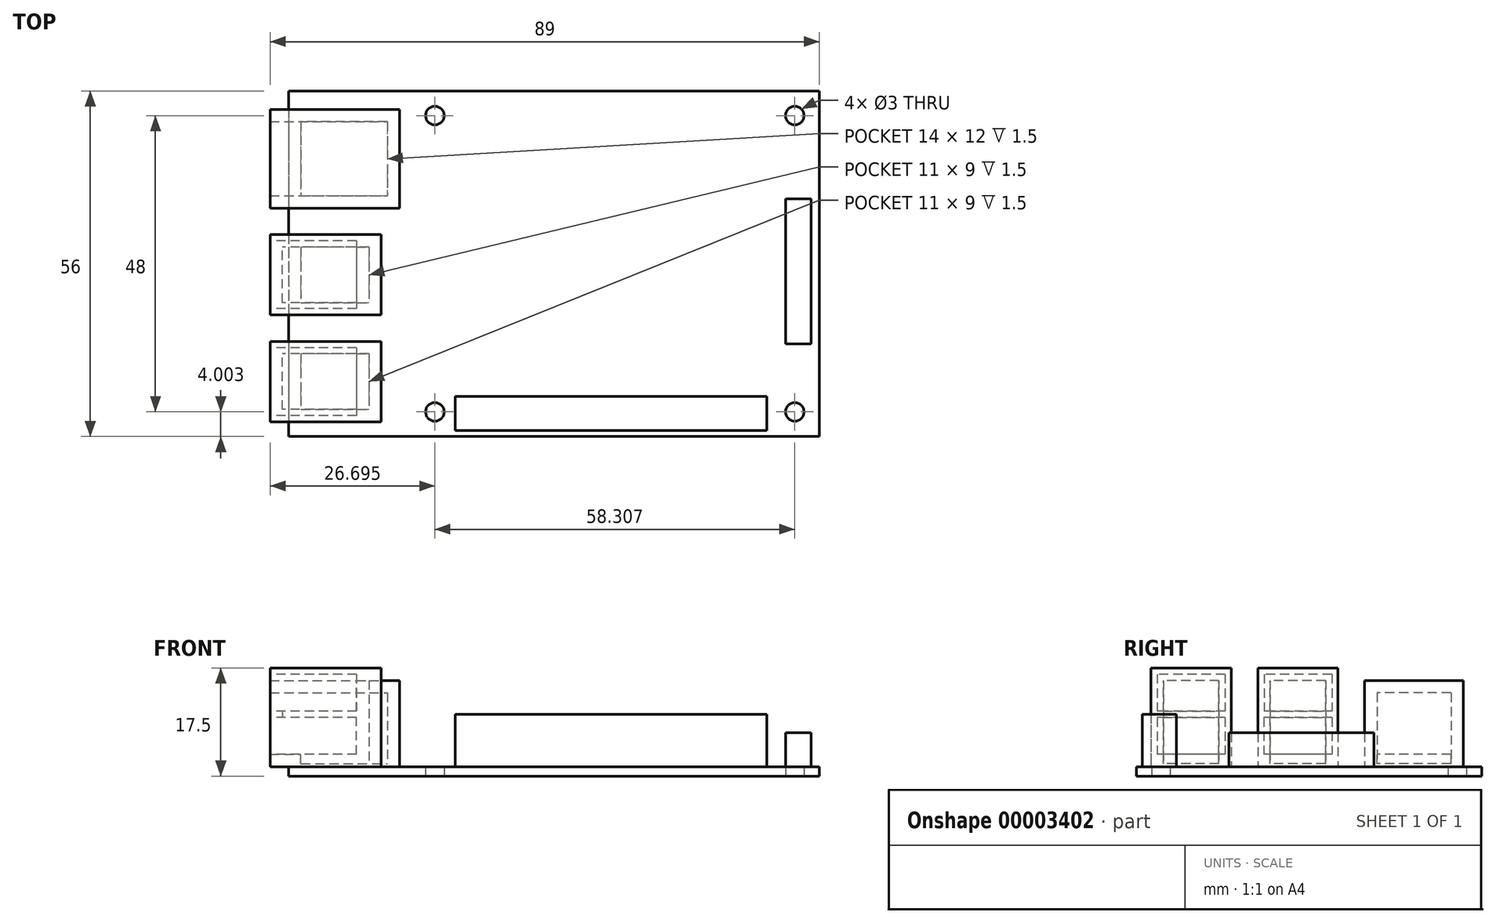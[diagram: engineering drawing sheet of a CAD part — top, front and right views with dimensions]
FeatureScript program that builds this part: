
annotation { "Feature Type Name" : "Feature", "Feature Type Description" : "" }
export const myFeature = defineFeature(function(context is Context, id is Id, definition is map)
    precondition{}
    {
        {
            var Q0;
            Q0=qCreatedBy(makeId("Top.planeOp"),FACE);
            var sketch = newSketch(context, id + "F0", { "sketchPlane" : qUnion([Q0])});
            skLineSegment(sketch, "E0.bottom", {"start": v(-78.39, -16) * mm, "end": v(7.61, -16) * mm});
            skLineSegment(sketch, "E0.top", {"start": v(-78.39, -72) * mm, "end": v(7.61, -72) * mm});
            skLineSegment(sketch, "E0.left", {"start": v(-78.39, -16) * mm, "end": v(-78.39, -72) * mm});
            skLineSegment(sketch, "E0.right", {"start": v(7.61, -16) * mm, "end": v(7.61, -72) * mm});
            skCircle(sketch, "E1", {"center": v(3.61, -20) * mm, "radius": 3 * mm, "construction": true});
            skCircle(sketch, "E2", {"center": v(3.61, -20) * mm, "radius": 1.5 * mm});
            skCircle(sketch, "E3.0.MirrorC", {"center": v(3.61, -68) * mm, "radius": 1.5 * mm});
            skCircle(sketch, "E3.1.MirrorC", {"center": v(3.61, -68) * mm, "radius": 3 * mm, "construction": true});
            skCircle(sketch, "E4.0.MirrorC", {"center": v(-54.7, -68) * mm, "radius": 3 * mm, "construction": true});
            skCircle(sketch, "E4.1.MirrorC", {"center": v(-54.7, -68) * mm, "radius": 1.5 * mm});
            skCircle(sketch, "E4.2.MirrorC", {"center": v(-54.7, -20) * mm, "radius": 1.5 * mm});
            skCircle(sketch, "E4.3.MirrorC", {"center": v(-54.7, -20) * mm, "radius": 3 * mm, "construction": true});
            skSolve(sketch);
        }
        {
            var Q0;
            Q0=makeQuery(id+"F0.imprint","IMPRINT",FACE,{"disambiguationData":[TD([[makeQuery(id+"F0.imprint","IMPRINT",EDGE,{"derivedFrom":sQuery(id+"F0.wireOp",EDGE,"E0.bottom")}),-1.0]])]});
            extrude(context, id + "F1", {"entities" : qUnion([Q0]), "depth" : 1.5 * mm});
        }
        {
            var Q0;
            Q0=makeQuery(id+"F1.opExtrude","CAP_FACE",FACE,{"disambiguationData":[OSD([sQuery(id+"F0.wireOp",EDGE,"E0.bottom"),sQuery(id+"F0.wireOp",EDGE,"E0.top"),sQuery(id+"F0.wireOp",EDGE,"E0.left"),sQuery(id+"F0.wireOp",EDGE,"E0.right"),sQuery(id+"F0.wireOp",EDGE,"E2"),sQuery(id+"F0.wireOp",EDGE,"E3.0.MirrorC"),sQuery(id+"F0.wireOp",EDGE,"E4.1.MirrorC"),sQuery(id+"F0.wireOp",EDGE,"E4.2.MirrorC")])],"isStart":false});
            var sketch = newSketch(context, id + "F2", { "sketchPlane" : qUnion([Q0])});
            skLineSegment(sketch, "E5.bottom", {"start": v(-81.39, -19) * mm, "end": v(-60.39, -19) * mm});
            skLineSegment(sketch, "E5.top", {"start": v(-81.39, -35) * mm, "end": v(-60.39, -35) * mm});
            skLineSegment(sketch, "E5.left", {"start": v(-81.39, -19) * mm, "end": v(-81.39, -35) * mm});
            skLineSegment(sketch, "E5.right", {"start": v(-60.39, -19) * mm, "end": v(-60.39, -35) * mm});
            skLineSegment(sketch, "E6.bottom", {"start": v(-81.39, -56.6) * mm, "end": v(-63.39, -56.6) * mm});
            skLineSegment(sketch, "E6.top", {"start": v(-81.39, -69.6) * mm, "end": v(-63.39, -69.6) * mm});
            skLineSegment(sketch, "E6.left", {"start": v(-81.39, -56.6) * mm, "end": v(-81.39, -69.6) * mm});
            skLineSegment(sketch, "E6.right", {"start": v(-63.39, -56.6) * mm, "end": v(-63.39, -69.6) * mm});
            skLineSegment(sketch, "E7.bottom", {"start": v(-81.39, -39.3) * mm, "end": v(-63.39, -39.3) * mm});
            skLineSegment(sketch, "E7.top", {"start": v(-81.39, -52.3) * mm, "end": v(-63.39, -52.3) * mm});
            skLineSegment(sketch, "E7.left", {"start": v(-81.39, -39.3) * mm, "end": v(-81.39, -52.3) * mm});
            skLineSegment(sketch, "E7.right", {"start": v(-63.39, -39.3) * mm, "end": v(-63.39, -52.3) * mm});
            skSolve(sketch);
        }
        {
            var Q0;
            {var subQ5=sQuery(id+"F2.wireOp",EDGE,"E5.right");Q0=makeQuery(id+"F2.imprint","IMPRINT",FACE,{"disambiguationData":[TD([[makeQuery(id+"F2.imprint","IMPRINT",EDGE,{"derivedFrom":subQ5}),-1.0]])]});}
            var Q1;
            {var subQ5=sQuery(id+"F2.wireOp",EDGE,"E5.left");Q1=makeQuery(id+"F2.imprint","IMPRINT",FACE,{"disambiguationData":[TD([[makeQuery(id+"F2.imprint","IMPRINT",EDGE,{"derivedFrom":subQ5}),1.0]])]});}
            extrude(context, id + "F3", {"entities" : qUnion([Q0, Q1]), "operationType" : NewBodyOperationType.ADD, "depth" : 14 * mm});
        }
        {
            var Q0;
            {var subQ5=sQuery(id+"F2.wireOp",EDGE,"E6.right");Q0=makeQuery(id+"F2.imprint","IMPRINT",FACE,{"disambiguationData":[TD([[makeQuery(id+"F2.imprint","IMPRINT",EDGE,{"derivedFrom":subQ5}),-1.0]])]});}
            var Q1;
            {var subQ5=sQuery(id+"F2.wireOp",EDGE,"E7.right");Q1=makeQuery(id+"F2.imprint","IMPRINT",FACE,{"disambiguationData":[TD([[makeQuery(id+"F2.imprint","IMPRINT",EDGE,{"derivedFrom":subQ5}),-1.0]])]});}
            var Q2;
            {var subQ5=sQuery(id+"F2.wireOp",EDGE,"E7.left");Q2=makeQuery(id+"F2.imprint","IMPRINT",FACE,{"disambiguationData":[TD([[makeQuery(id+"F2.imprint","IMPRINT",EDGE,{"derivedFrom":subQ5}),1.0]])]});}
            var Q3;
            {var subQ5=sQuery(id+"F2.wireOp",EDGE,"E6.left");Q3=makeQuery(id+"F2.imprint","IMPRINT",FACE,{"disambiguationData":[TD([[makeQuery(id+"F2.imprint","IMPRINT",EDGE,{"derivedFrom":subQ5}),1.0]])]});}
            extrude(context, id + "F4", {"entities" : qUnion([Q0, Q1, Q2, Q3]), "operationType" : NewBodyOperationType.ADD, "depth" : 16 * mm});
        }
        {
            var Q0;
            Q0=makeQuery(id+"F3.opExtrude","SWEPT_FACE",FACE,{"disambiguationData":[OSD([sQuery(id+"F2.wireOp",EDGE,"E5.left")])]});
            shell(context, id + "F5", {"entities" : qUnion([Q0]), "thickness" : 2 * mm});
        }
        {
            var Q0;
            {var subQ15=sQuery(id+"F2.wireOp",EDGE,"E5.right");Q0=makeQuery(id+"F2.imprint","IMPRINT",FACE,{"disambiguationData":[TD([[makeQuery(id+"F2.imprint","IMPRINT",EDGE,{"derivedFrom":subQ15}),1.0]])]});}
            var sketch = newSketch(context, id + "F6", { "sketchPlane" : qUnion([Q0])});
            skLineSegment(sketch, "E8.bottom", {"start": v(-51.39, -65.5) * mm, "end": v(-0.89, -65.5) * mm});
            skLineSegment(sketch, "E8.top", {"start": v(-51.39, -71) * mm, "end": v(-0.89, -71) * mm});
            skLineSegment(sketch, "E8.left", {"start": v(-51.39, -65.5) * mm, "end": v(-51.39, -71) * mm});
            skLineSegment(sketch, "E8.right", {"start": v(-0.89, -65.5) * mm, "end": v(-0.89, -71) * mm});
            skLineSegment(sketch, "E9.bottom", {"start": v(2.11, -33.5) * mm, "end": v(6.23, -33.5) * mm});
            skLineSegment(sketch, "E9.top", {"start": v(2.11, -56.97) * mm, "end": v(6.23, -56.97) * mm});
            skLineSegment(sketch, "E9.left", {"start": v(2.11, -33.5) * mm, "end": v(2.11, -56.97) * mm});
            skLineSegment(sketch, "E9.right", {"start": v(6.23, -33.5) * mm, "end": v(6.23, -56.97) * mm});
            skSolve(sketch);
        }
        {
            var Q0;
            Q0=makeQuery(id+"F6.imprint","IMPRINT",FACE,{"disambiguationData":[TD([[makeQuery(id+"F6.imprint","IMPRINT",EDGE,{"derivedFrom":sQuery(id+"F6.wireOp",EDGE,"E9.bottom")}),-1.0]])]});
            extrude(context, id + "F7", {"entities" : qUnion([Q0]), "operationType" : NewBodyOperationType.ADD, "depth" : 5.5 * mm});
        }
        {
            var Q0;
            Q0=makeQuery(id+"F6.imprint","IMPRINT",FACE,{"disambiguationData":[TD([[makeQuery(id+"F6.imprint","IMPRINT",EDGE,{"derivedFrom":sQuery(id+"F6.wireOp",EDGE,"E8.bottom")}),-1.0]])]});
            extrude(context, id + "F8", {"entities" : qUnion([Q0]), "operationType" : NewBodyOperationType.ADD, "depth" : 8.5 * mm});
        }
        {
            var Q0;
            Q0=makeQuery(id+"F4.opExtrude","SWEPT_FACE",FACE,{"disambiguationData":[OSD([sQuery(id+"F2.wireOp",EDGE,"E7.left")])]});
            var sketch = newSketch(context, id + "F9", { "sketchPlane" : qUnion([Q0])});
            skLineSegment(sketch, "E10.bottom", {"start": v(40.3, 16.5) * mm, "end": v(51.3, 16.5) * mm});
            skLineSegment(sketch, "E10.top", {"start": v(40.3, 10.5) * mm, "end": v(51.3, 10.5) * mm});
            skLineSegment(sketch, "E10.left", {"start": v(40.3, 16.5) * mm, "end": v(40.3, 10.5) * mm});
            skLineSegment(sketch, "E10.right", {"start": v(51.3, 16.5) * mm, "end": v(51.3, 10.5) * mm});
            skLineSegment(sketch, "E11.1.0.0", {"start": v(40.3, 3.5) * mm, "end": v(51.3, 3.5) * mm});
            skLineSegment(sketch, "E11.1.0.1", {"start": v(40.3, 9.5) * mm, "end": v(40.3, 3.5) * mm});
            skLineSegment(sketch, "E11.1.0.2", {"start": v(40.3, 9.5) * mm, "end": v(51.3, 9.5) * mm});
            skLineSegment(sketch, "E11.1.0.3", {"start": v(51.3, 9.5) * mm, "end": v(51.3, 3.5) * mm});
            skLineSegment(sketch, "E11.direction1", {"start": v(40.3, 10.5) * mm, "end": v(40.3, 3.5) * mm, "construction": true});
            skLineSegment(sketch, "E12.1.0.0", {"start": v(68.6, 16.5) * mm, "end": v(68.6, 10.5) * mm});
            skLineSegment(sketch, "E12.1.0.1", {"start": v(57.6, 16.5) * mm, "end": v(68.6, 16.5) * mm});
            skLineSegment(sketch, "E12.1.0.2", {"start": v(57.6, 3.5) * mm, "end": v(68.6, 3.5) * mm});
            skLineSegment(sketch, "E12.1.0.3", {"start": v(57.6, 10.5) * mm, "end": v(68.6, 10.5) * mm});
            skLineSegment(sketch, "E12.1.0.4", {"start": v(57.6, 16.5) * mm, "end": v(57.6, 10.5) * mm});
            skLineSegment(sketch, "E12.1.0.5", {"start": v(57.6, 9.5) * mm, "end": v(68.6, 9.5) * mm});
            skLineSegment(sketch, "E12.1.0.6", {"start": v(68.6, 9.5) * mm, "end": v(68.6, 3.5) * mm});
            skLineSegment(sketch, "E12.1.0.8", {"start": v(57.6, 9.5) * mm, "end": v(57.6, 3.5) * mm});
            skSolve(sketch);
        }
        {
            var Q0;
            Q0=makeQuery(id+"F9.imprint","IMPRINT",FACE,{"disambiguationData":[TD([[makeQuery(id+"F9.imprint","IMPRINT",EDGE,{"derivedFrom":sQuery(id+"F9.wireOp",EDGE,"E10.bottom")}),-1.0]])]});
            var Q1;
            Q1=makeQuery(id+"F9.imprint","IMPRINT",FACE,{"disambiguationData":[TD([[makeQuery(id+"F9.imprint","IMPRINT",EDGE,{"derivedFrom":sQuery(id+"F9.wireOp",EDGE,"E11.1.0.0")}),1.0]])]});
            var Q2;
            Q2=makeQuery(id+"F9.imprint","IMPRINT",FACE,{"disambiguationData":[TD([[makeQuery(id+"F9.imprint","IMPRINT",EDGE,{"derivedFrom":sQuery(id+"F9.wireOp",EDGE,"E12.1.0.2")}),1.0]])]});
            var Q3;
            Q3=makeQuery(id+"F9.imprint","IMPRINT",FACE,{"disambiguationData":[TD([[makeQuery(id+"F9.imprint","IMPRINT",EDGE,{"derivedFrom":sQuery(id+"F9.wireOp",EDGE,"E12.1.0.0")}),-1.0]])]});
            extrude(context, id + "F10", {"entities" : qUnion([Q0, Q1, Q2, Q3]), "operationType" : NewBodyOperationType.REMOVE, "oppositeDirection" : true, "depth" : 14 * mm});
        }
    });
